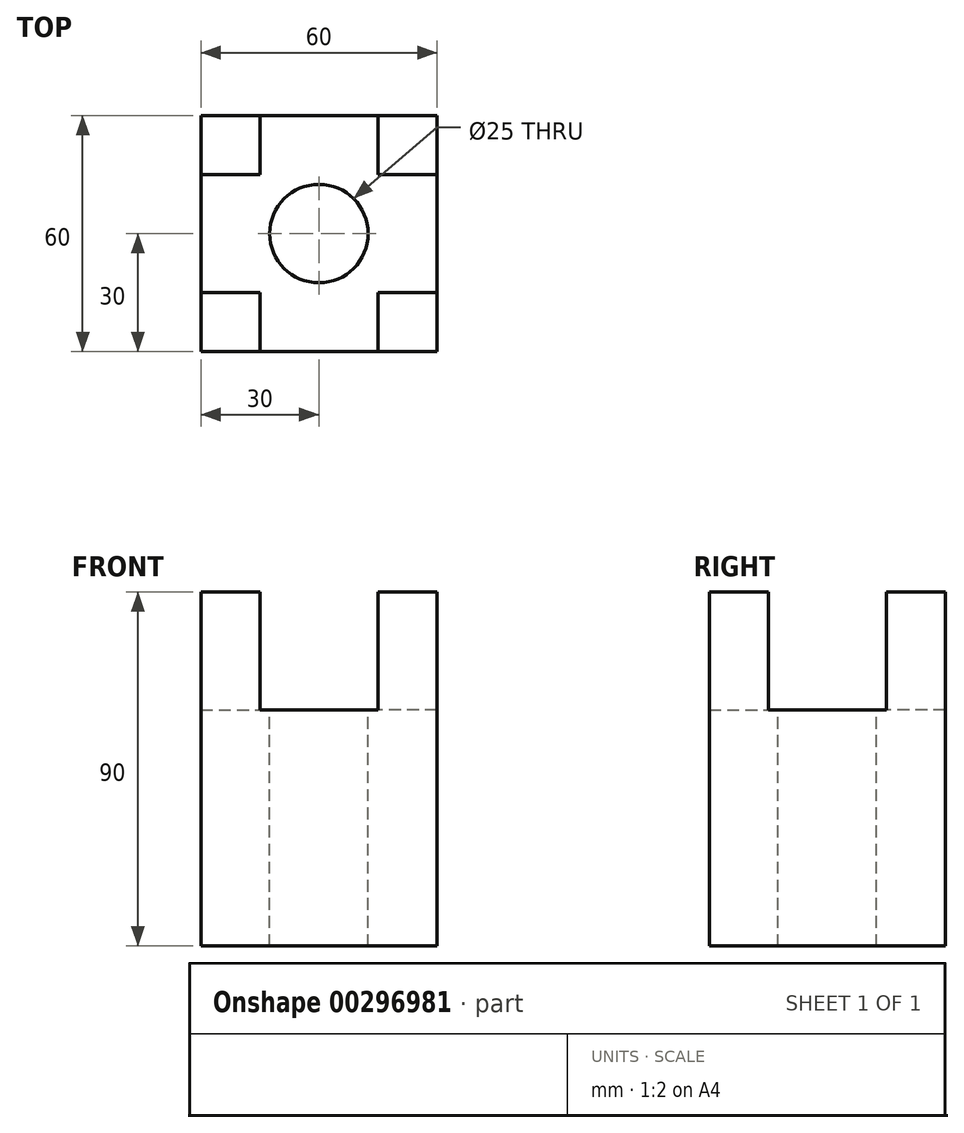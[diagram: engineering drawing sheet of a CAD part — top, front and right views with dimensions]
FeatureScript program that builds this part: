
annotation { "Feature Type Name" : "Feature", "Feature Type Description" : "" }
export const myFeature = defineFeature(function(context is Context, id is Id, definition is map)
    precondition{}
    {
        {
            var Q0;
            Q0=qCreatedBy(makeId("Top.planeOp"),FACE);
            var sketch = newSketch(context, id + "F0", { "sketchPlane" : qUnion([Q0])});
            skLineSegment(sketch, "E0.bottom", {"start": v(30, -30) * mm, "end": v(-30, -30) * mm});
            skLineSegment(sketch, "E0.top", {"start": v(30, 30) * mm, "end": v(-30, 30) * mm});
            skLineSegment(sketch, "E0.left", {"start": v(30, -30) * mm, "end": v(30, 30) * mm});
            skLineSegment(sketch, "E0.right", {"start": v(-30, -30) * mm, "end": v(-30, 30) * mm});
            skPoint(sketch, "E0.middle", {"position": v(0, 0) * mm});
            skSolve(sketch);
        }
        {
            var Q0;
            Q0=makeQuery(id+"F0.imprint","IMPRINT",FACE,{"disambiguationData":[TD([[makeQuery(id+"F0.imprint","IMPRINT",EDGE,{"derivedFrom":sQuery(id+"F0.wireOp",EDGE,"E0.bottom")}),-1.0]])]});
            extrude(context, id + "F1", {"entities" : qUnion([Q0]), "depth" : 60 * mm});
        }
        {
            var Q0;
            Q0=makeQuery(id+"F1.opExtrude","CAP_FACE",FACE,{"disambiguationData":[OSD([sQuery(id+"F0.wireOp",EDGE,"E0.bottom"),sQuery(id+"F0.wireOp",EDGE,"E0.top"),sQuery(id+"F0.wireOp",EDGE,"E0.left"),sQuery(id+"F0.wireOp",EDGE,"E0.right")])],"isStart":false});
            var sketch = newSketch(context, id + "F2", { "sketchPlane" : qUnion([Q0])});
            skLineSegment(sketch, "E1.bottom", {"start": v(-30, 30) * mm, "end": v(-15, 30) * mm});
            skLineSegment(sketch, "E1.top", {"start": v(-30, 15) * mm, "end": v(-15, 15) * mm});
            skLineSegment(sketch, "E1.left", {"start": v(-30, 30) * mm, "end": v(-30, 15) * mm});
            skLineSegment(sketch, "E1.right", {"start": v(-15, 30) * mm, "end": v(-15, 15) * mm});
            skLineSegment(sketch, "E2.bottom", {"start": v(30, 30) * mm, "end": v(15, 30) * mm});
            skLineSegment(sketch, "E2.top", {"start": v(30, 15) * mm, "end": v(15, 15) * mm});
            skLineSegment(sketch, "E2.left", {"start": v(30, 30) * mm, "end": v(30, 15) * mm});
            skLineSegment(sketch, "E2.right", {"start": v(15, 30) * mm, "end": v(15, 15) * mm});
            skLineSegment(sketch, "E3.bottom", {"start": v(30, -30) * mm, "end": v(15, -30) * mm});
            skLineSegment(sketch, "E3.top", {"start": v(30, -15) * mm, "end": v(15, -15) * mm});
            skLineSegment(sketch, "E3.left", {"start": v(30, -30) * mm, "end": v(30, -15) * mm});
            skLineSegment(sketch, "E3.right", {"start": v(15, -30) * mm, "end": v(15, -15) * mm});
            skLineSegment(sketch, "E4.bottom", {"start": v(-30, -30) * mm, "end": v(-15, -30) * mm});
            skLineSegment(sketch, "E4.top", {"start": v(-30, -15) * mm, "end": v(-15, -15) * mm});
            skLineSegment(sketch, "E4.left", {"start": v(-30, -30) * mm, "end": v(-30, -15) * mm});
            skLineSegment(sketch, "E4.right", {"start": v(-15, -30) * mm, "end": v(-15, -15) * mm});
            skSolve(sketch);
        }
        {
            var Q0;
            Q0=makeQuery(id+"F2.imprint","IMPRINT",FACE,{"disambiguationData":[TD([[makeQuery(id+"F2.imprint","IMPRINT",EDGE,{"derivedFrom":sQuery(id+"F2.wireOp",EDGE,"E4.bottom")}),-1.0]])]});
            var Q1;
            Q1=makeQuery(id+"F2.imprint","IMPRINT",FACE,{"disambiguationData":[TD([[makeQuery(id+"F2.imprint","IMPRINT",EDGE,{"derivedFrom":sQuery(id+"F2.wireOp",EDGE,"E1.bottom")}),1.0]])]});
            var Q2;
            Q2=makeQuery(id+"F2.imprint","IMPRINT",FACE,{"disambiguationData":[TD([[makeQuery(id+"F2.imprint","IMPRINT",EDGE,{"derivedFrom":sQuery(id+"F2.wireOp",EDGE,"E2.bottom")}),1.0]])]});
            var Q3;
            Q3=makeQuery(id+"F2.imprint","IMPRINT",FACE,{"disambiguationData":[TD([[makeQuery(id+"F2.imprint","IMPRINT",EDGE,{"derivedFrom":sQuery(id+"F2.wireOp",EDGE,"E3.bottom")}),-1.0]])]});
            extrude(context, id + "F3", {"entities" : qUnion([Q0, Q1, Q2, Q3]), "operationType" : NewBodyOperationType.ADD, "depth" : 30 * mm});
        }
        {
            var Q0;
            Q0=makeQuery(id+"F1.opExtrude","CAP_FACE",FACE,{"disambiguationData":[OSD([sQuery(id+"F0.wireOp",EDGE,"E0.bottom"),sQuery(id+"F0.wireOp",EDGE,"E0.top"),sQuery(id+"F0.wireOp",EDGE,"E0.left"),sQuery(id+"F0.wireOp",EDGE,"E0.right")])],"isStart":false});
            var sketch = newSketch(context, id + "F4", { "sketchPlane" : qUnion([Q0])});
            skCircle(sketch, "E5", {"center": v(0, 0) * mm, "radius": 12.5 * mm});
            skSolve(sketch);
        }
        {
            var Q0;
            Q0=makeQuery(id+"F4.imprint","IMPRINT",FACE,{"disambiguationData":[TD([[makeQuery(id+"F4.imprint","IMPRINT",EDGE,{"derivedFrom":sQuery(id+"F4.wireOp",EDGE,"E5")}),1.0]])]});
            extrude(context, id + "F5", {"entities" : qUnion([Q0]), "operationType" : NewBodyOperationType.REMOVE, "oppositeDirection" : true, "depth" : 60 * mm});
        }
    });
